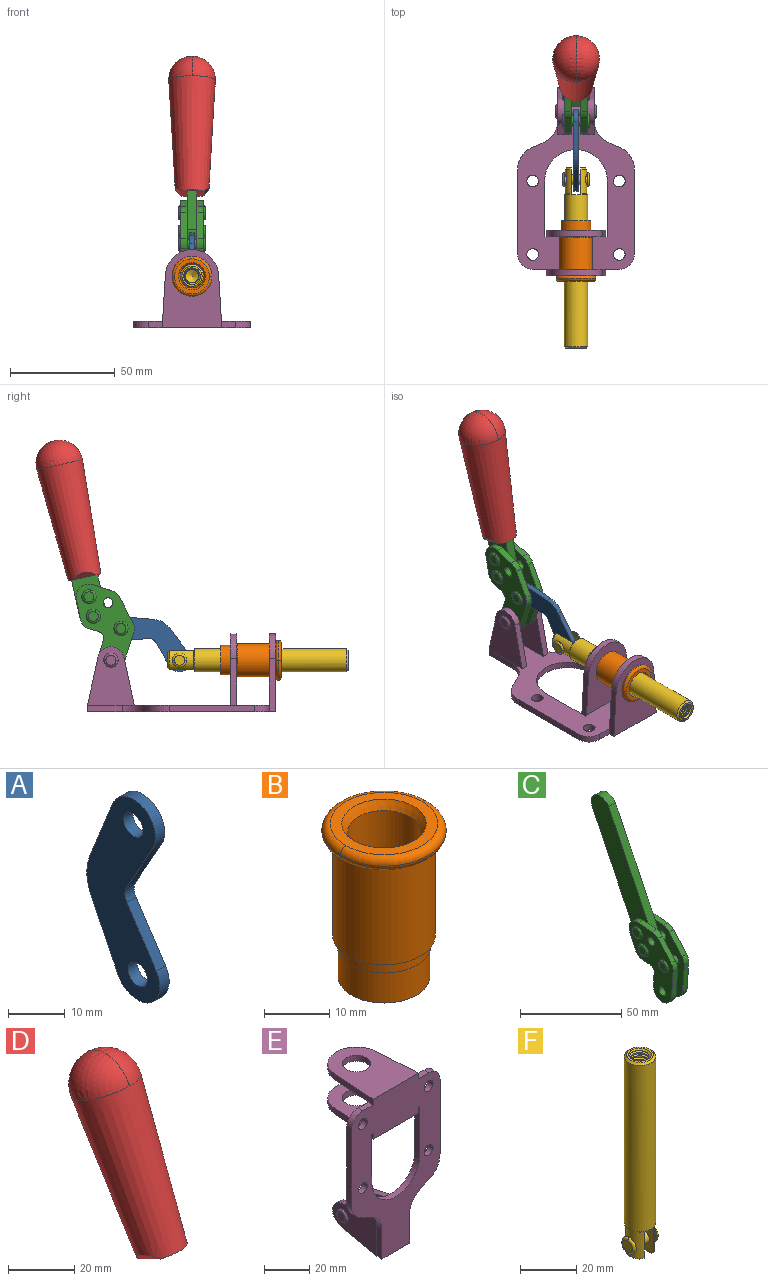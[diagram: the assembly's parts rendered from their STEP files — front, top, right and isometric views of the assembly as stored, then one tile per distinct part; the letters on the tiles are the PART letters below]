
ASSEMBLY  parts=6 mates=6
PART A: 12 faces, bbox 2.3x18.2x42.8 mm
  f0: cylinder r=2.4mm len=4.8mm, axis (1,0,0), area 34.9mm2, adj f4,f11
  f1: cylinder r=10.41mm len=8.47mm, axis (1,0,0), area 20.2mm2, adj f4,f9,f10,f11
  f2: cylinder r=3.05mm len=3.16mm, axis (1,0,0), area 7.7mm2, adj f4,f6,f7,f11
  f3: cylinder r=2.4mm len=4.8mm, axis (1,0,0), area 34.9mm2, adj f4,f11
  f4: plane 42.81x18.23mm, normal (-1,0,0), area 414.1mm2, adj f0,f1,f2,f3,f5,f6,f7,f8
  f5: cylinder r=5.54mm len=10.67mm, axis (1,0,0), area 41.8mm2, adj f4,f6,f10,f11
  f6: plane 11.66x6.53mm, normal (0,-0.87,-0.49), area 30.9mm2, adj f2,f4,f5,f11
  f7: plane 11.17x7.33mm, normal (0,-0.84,0.55), area 30.9mm2, adj f2,f4,f8,f11
  f8: cylinder r=5.54mm len=10.51mm, axis (1,0,0), area 41.8mm2, adj f4,f7,f9,f11
  f9: plane 13.67x6.67mm, normal (0,0.9,-0.44), area 35.1mm2, adj f1,f4,f8,f11
  f10: plane 14.1x5.7mm, normal (0,0.93,0.37), area 35.1mm2, adj f1,f4,f5,f11
  f11: plane 42.81x18.23mm, normal (1,0,0), area 414.1mm2, adj f0,f1,f2,f3,f5,f6,f7,f8
PART B: 15 faces, bbox 20.6x20.6x28.7 mm
  f0: torus R=8.26mm, axis (0,0,1), area 56.8mm2, adj f1,f10,f12
  f1: torus R=8.26mm, axis (0,0,1), area 56.8mm2, adj f0,f6,f13
  f2: cylinder r=5.59mm len=25.91mm, axis (0,0,1), area 909.6mm2, adj f3,f4
  f3: cone r=6.86mm half-angle=45deg, axis (0,0,-1), area 70.2mm2, adj f2,f14
  f4: cone r=6.47mm half-angle=30deg, axis (0,0,1), area 66.7mm2, adj f2,f13
  f5: cylinder r=7.04mm len=14.07mm, axis (0,0,1), area 252.6mm2, adj f11,f14
  f6: torus R=8.26mm, axis (0,0,1), area 56.8mm2, adj f1,f12,f13
  f7: cylinder r=7.16mm len=14.33mm, axis (0,0,1), area 91.5mm2, adj f9,f11
  f8: cylinder r=7.86mm len=18.42mm, axis (0,0,1), area 909.6mm2, adj f9,f10
  f9: plane 15.72x15.72mm, normal (0,0,-1), area 33mm2, adj f7,f8
  f10: plane 16.51x16.51mm, normal (0,0,-1), area 19.9mm2, adj f0,f8,f12
  f11: plane 14.33x14.33mm, normal (0,0,-1), area 5.7mm2, adj f5,f7
  f12: torus R=8.26mm, axis (0,0,1), area 56.8mm2, adj f0,f6,f10
  f13: plane 16.51x16.51mm, normal (0,0,1), area 82.7mm2, adj f1,f4,f6
  f14: plane 14.07x14.07mm, normal (0,0,-1), area 7.8mm2, adj f3,f5
PART C: 59 faces, bbox 12.9x60.2x99.6 mm
  f0: torus R=2.39mm, axis (-1,0,0), area 14.9mm2, adj f20,f43,f51
  f1: torus R=2.39mm, axis (-1,0,0), area 14.9mm2, adj f19,f42,f51
  f2: torus R=2.39mm, axis (-1,0,0), area 14.9mm2, adj f18,f35,f51
  f3: torus R=2.39mm, axis (-1,0,0), area 14.9mm2, adj f14,f17,f23
  f4: torus R=2.39mm, axis (-1,0,0), area 14.9mm2, adj f13,f16,f23
  f5: torus R=2.39mm, axis (-1,0,0), area 14.9mm2, adj f12,f15,f23
  f6: cylinder r=2.39mm len=4.78mm, axis (1,0,0), area 46.5mm2, adj f48,f50,f51
  f7: cylinder r=2.39mm len=4.78mm, axis (1,0,0), area 46.5mm2, adj f50,f51
  f8: cylinder r=6.35mm len=12.68mm, axis (1,0,0), area 61.8mm2, adj f38,f39,f50,f51
  f9: cylinder r=2.39mm len=4.78mm, axis (-1,0,0), area 70.5mm2, adj f46,f50
  f10: cylinder r=2.39mm len=4.78mm, axis (-1,0,0), area 46.5mm2, adj f23,f45,f46
  f11: cylinder r=2.39mm len=4.78mm, axis (-1,0,0), area 46.5mm2, adj f23,f46
  f12: plane 4.78x4.78mm, normal (1,0,0), area 17.9mm2, adj f5,f15
  f13: plane 4.78x4.78mm, normal (1,0,0), area 17.9mm2, adj f4,f16
  f14: plane 4.78x4.78mm, normal (1,0,0), area 17.9mm2, adj f3,f17
  f15: torus R=2.39mm, axis (-1,0,0), area 14.9mm2, adj f5,f12,f23
  f16: torus R=2.39mm, axis (-1,0,0), area 14.9mm2, adj f4,f13,f23
  f17: torus R=2.39mm, axis (-1,0,0), area 14.9mm2, adj f3,f14,f23
  f18: plane 4.78x4.78mm, normal (-1,0,0), area 17.9mm2, adj f2,f35
  f19: plane 4.78x4.78mm, normal (-1,0,0), area 17.9mm2, adj f1,f42
  f20: plane 4.78x4.78mm, normal (-1,0,0), area 17.9mm2, adj f0,f43
  f21: plane 2.26x0.2mm, normal (1,0,0), area 0.2mm2, adj f31,f44
  f22: plane 2.26x0.2mm, normal (-1,0,0), area 0.2mm2, adj f41,f44
  f23: plane 39.37x30.77mm, normal (1,0,0), area 565.5mm2, adj f3,f4,f5,f10,f11,f15,f16,f17
  f24: cylinder r=6.1mm len=4.15mm, axis (-1,0,0), area 14.7mm2, adj f23,f25,f32,f46
  f25: plane 10.25x9.01mm, normal (0,-0.75,0.66), area 42.3mm2, adj f23,f24,f26,f46
  f26: cylinder r=6.35mm len=4.64mm, axis (-1,0,0), area 15.6mm2, adj f23,f25,f27,f46
  f27: plane 15.84x3.1mm, normal (0,-1,-0.07), area 49.2mm2, adj f23,f26,f28,f46
  f28: cylinder r=6.35mm len=12.68mm, axis (-1,0,0), area 61.8mm2, adj f23,f27,f29,f46
  f29: plane 8.11x3.1mm, normal (0,1,0.07), area 25.2mm2, adj f23,f28,f30,f46
  f30: cylinder r=3.05mm len=3.25mm, axis (-1,0,0), area 14.8mm2, adj f23,f29,f31,f46
  f31: plane 5.99x3.1mm, normal (0,0.07,-1), area 18.6mm2, adj f21,f23,f30,f44,f46
  f32: plane 9.5x3.1mm, normal (0,-0.07,1), area 29.5mm2, adj f23,f24,f33,f46,f47
  f33: cylinder r=6.1mm len=8.63mm, axis (-1,0,0), area 39.1mm2, adj f23,f32,f34,f47
  f34: plane 8.65x3.96mm, normal (0,0.91,-0.42), area 29.5mm2, adj f23,f33,f44,f47
  f35: torus R=2.39mm, axis (-1,0,0), area 14.9mm2, adj f2,f18,f51
  f36: plane 10.25x9.01mm, normal (0,-0.75,0.66), area 42.3mm2, adj f37,f49,f50,f51
  f37: cylinder r=6.35mm len=4.64mm, axis (1,0,0), area 15.6mm2, adj f36,f38,f50,f51
  f38: plane 15.84x3.1mm, normal (0,-1,-0.07), area 49.2mm2, adj f8,f37,f50,f51
  f39: plane 8.11x3.1mm, normal (0,1,0.07), area 25.2mm2, adj f8,f40,f50,f51
  f40: cylinder r=3.05mm len=3.25mm, axis (1,0,0), area 14.8mm2, adj f39,f41,f50,f51
  f41: plane 5.99x3.1mm, normal (0,0.07,-1), area 18.6mm2, adj f22,f40,f44,f50,f51
  f42: torus R=2.39mm, axis (-1,0,0), area 14.9mm2, adj f1,f19,f51
  f43: torus R=2.39mm, axis (-1,0,0), area 14.9mm2, adj f0,f20,f51
  f44: cylinder r=6.35mm len=12.12mm, axis (-1,0,0), area 128.9mm2, adj f21,f22,f23,f31,f34,f41,f46,f47
  f45: plane 2.65x1.35mm, normal (1,0,0), area 1mm2, adj f10,f55
  f46: plane 39.08x20.42mm, normal (-1,0,0), area 412.5mm2, adj f9,f10,f11,f24,f25,f26,f27,f28
  f47: plane 77.62x39.82mm, normal (1,0,0), area 850mm2, adj f32,f33,f34,f44,f53,f54,f55
  f48: plane 2.65x1.35mm, normal (-1,0,0), area 1mm2, adj f6,f55
  f49: cylinder r=6.1mm len=4.15mm, axis (1,0,0), area 14.7mm2, adj f36,f50,f51,f56
  f50: plane 39.08x20.42mm, normal (1,0,0), area 412.5mm2, adj f6,f7,f8,f9,f36,f37,f38,f39
  f51: plane 39.37x30.77mm, normal (-1,0,0), area 565.5mm2, adj f0,f1,f2,f6,f7,f8,f35,f36
  f52: plane 8.65x3.96mm, normal (0,0.91,-0.42), area 29.5mm2, adj f44,f51,f57,f58
  f53: plane 68.49x33.4mm, normal (0,0.9,-0.44), area 358.1mm2, adj f44,f47,f54,f58
  f54: cylinder r=6.35mm len=12.06mm, axis (1,0,0), area 93.7mm2, adj f47,f53,f55,f58
  f55: plane 68.49x33.4mm, normal (0,-0.9,0.44), area 358.1mm2, adj f44,f45,f46,f47,f48,f50,f54,f58
  f56: plane 9.5x3.1mm, normal (0,-0.07,1), area 29.5mm2, adj f49,f50,f51,f57,f58
  f57: cylinder r=6.1mm len=8.63mm, axis (1,0,0), area 39.1mm2, adj f51,f52,f56,f58
  f58: plane 77.62x39.82mm, normal (-1,0,0), area 850mm2, adj f44,f52,f53,f54,f55,f56,f57
PART D: 11 faces, bbox 22.3x42.6x64.5 mm
  f0: sphere r=11.13mm, area 411.4mm2, adj f1,f8
  f1: cone r=11.11mm half-angle=3.3deg, axis (0,0.44,0.9), area 3251.8mm2, adj f0,f7,f8,f9,f10
  f2: cylinder r=6.16mm len=11.7mm, axis (1,0,0), area 89.5mm2, adj f3,f4,f5,f6
  f3: plane 60.23x36.75mm, normal (-1,0,0), area 763.6mm2, adj f2,f4,f6,f10
  f4: plane 51.37x25.05mm, normal (0,0.9,-0.44), area 264.2mm2, adj f2,f3,f5,f10
  f5: plane 60.23x36.75mm, normal (1,0,0), area 763.6mm2, adj f2,f4,f6,f10
  f6: plane 51.37x25.05mm, normal (0,-0.9,0.44), area 264.2mm2, adj f2,f3,f5,f10
  f7: plane 9.95x5.95mm, normal (0.71,-0.31,-0.64), area 25.8mm2, adj f1,f10
  f8: sphere r=11.13mm, area 411.4mm2, adj f0,f1
  f9: plane 9.95x5.95mm, normal (-0.71,-0.31,-0.64), area 25.8mm2, adj f1,f10
  f10: plane 14.27x11.38mm, normal (0,-0.44,-0.9), area 106.7mm2, adj f1,f3,f4,f5,f6,f7,f9
PART E: 55 faces, bbox 55.7x37.4x89.8 mm
  f0: torus R=2.41mm, axis (-1,0,0), area 15mm2, adj f11,f15,f25
  f1: torus R=2.41mm, axis (-1,0,0), area 15mm2, adj f10,f12,f22
  f2: cylinder r=2.78mm len=5.56mm, axis (0,-1,0), area 54.2mm2, adj f30,f54
  f3: cylinder r=14.99mm len=29.97mm, axis (0,-1,0), area 145.9mm2, adj f30,f49,f53,f54
  f4: cylinder r=2.78mm len=5.56mm, axis (0,-1,0), area 54.2mm2, adj f30,f54
  f5: cylinder r=2.78mm len=5.56mm, axis (0,-1,0), area 54.2mm2, adj f30,f54
  f6: cylinder r=2.78mm len=5.56mm, axis (0,-1,0), area 54.2mm2, adj f30,f54
  f7: cylinder r=6.35mm len=12.7mm, axis (0,0,1), area 123.6mm2, adj f27,f51
  f8: cylinder r=6.35mm len=12.7mm, axis (0,0,-1), area 124.7mm2, adj f21,f35
  f9: cylinder r=2.41mm len=11.18mm, axis (-1,0,0), area 169.4mm2, adj f16,f19
  f10: plane 4.83x4.83mm, normal (1,0,0), area 18.3mm2, adj f1,f12
  f11: plane 4.83x4.83mm, normal (-1,0,0), area 18.3mm2, adj f0,f15
  f12: torus R=2.41mm, axis (-1,0,0), area 15mm2, adj f1,f10,f22
  f13: cylinder r=6.35mm len=12.41mm, axis (1,0,0), area 53.4mm2, adj f18,f19,f22,f23
  f14: cylinder r=6.35mm len=12.41mm, axis (-1,0,0), area 53.4mm2, adj f16,f17,f24,f25
  f15: torus R=2.41mm, axis (-1,0,0), area 15mm2, adj f0,f11,f25
  f16: plane 27.86x22.35mm, normal (1,0,0), area 425.4mm2, adj f9,f14,f17,f24,f30
  f17: plane 22.86x4.97mm, normal (0,0.21,0.98), area 72.5mm2, adj f14,f16,f25,f30
  f18: plane 22.86x4.97mm, normal (0,0.21,0.98), area 72.5mm2, adj f13,f19,f22,f30
  f19: plane 27.86x22.35mm, normal (-1,0,0), area 425.4mm2, adj f9,f13,f18,f23,f30
  f20: cylinder r=12.7mm len=25.35mm, axis (0,0,-1), area 119.8mm2, adj f21,f34,f35,f36
  f21: plane 34.21x28.07mm, normal (0,0,-1), area 702.4mm2, adj f8,f20,f30,f34,f36
  f22: plane 27.96x22.45mm, normal (1,0,0), area 407.2mm2, adj f1,f12,f13,f18,f23,f30,f42,f43
  f23: plane 22.86x4.97mm, normal (0,0.21,-0.98), area 72.5mm2, adj f13,f19,f22,f44
  f24: plane 22.86x4.97mm, normal (0,0.21,-0.98), area 72.5mm2, adj f14,f16,f25,f44
  f25: plane 27.86x22.35mm, normal (-1,0,0), area 407.1mm2, adj f0,f14,f15,f17,f24,f30,f45,f46
  f26: plane 3.1x0.95mm, normal (0,0,-1), area 2.7mm2, adj f30,f49,f50,f54
  f27: plane 34.21x28.07mm, normal (0,0,1), area 702.4mm2, adj f7,f28,f30,f50,f52
  f28: cylinder r=12.7mm len=25.35mm, axis (0,0,1), area 118.8mm2, adj f27,f50,f51,f52
  f29: plane 3.1x0.95mm, normal (0,0,-1), area 2.7mm2, adj f30,f52,f53,f54
  f30: plane 86.54x55.63mm, normal (0,1,0), area 2362.9mm2, adj f2,f3,f4,f5,f6,f16,f17,f18
  f31: plane 40.56x3.1mm, normal (-1,0,0), area 125.7mm2, adj f30,f32,f48,f54
  f32: cylinder r=7.11mm len=7.11mm, axis (0,-1,0), area 34.6mm2, adj f30,f31,f33,f54
  f33: plane 6.67x3.1mm, normal (0,0,1), area 20.4mm2, adj f30,f32,f34,f54
  f34: plane 25.39x3.13mm, normal (-1,0.06,0), area 79.5mm2, adj f20,f21,f33,f35,f54
  f35: plane 37.31x28.45mm, normal (0,0,1), area 789.9mm2, adj f8,f20,f34,f36,f54
  f36: plane 25.39x3.13mm, normal (1,0.06,0), area 79.5mm2, adj f20,f21,f35,f37,f54
  f37: plane 6.67x3.1mm, normal (0,0,1), area 20.4mm2, adj f30,f36,f38,f54
  f38: cylinder r=7.11mm len=7.11mm, axis (0,-1,0), area 34.6mm2, adj f30,f37,f39,f54
  f39: plane 40.56x3.1mm, normal (1,0,0), area 125.7mm2, adj f30,f38,f40,f54
  f40: cylinder r=11.18mm len=10.16mm, axis (0,-1,0), area 39.5mm2, adj f30,f39,f41,f54
  f41: plane 6.09x3.1mm, normal (0.42,0,-0.91), area 20.8mm2, adj f30,f40,f42,f54
  f42: cylinder r=11.18mm len=9.41mm, axis (0,-1,0), area 37.2mm2, adj f22,f30,f41,f43,f54
  f43: plane 16.5x3.1mm, normal (1,0,0), area 51.1mm2, adj f22,f42,f44,f54
  f44: plane 17.37x3.1mm, normal (0,0,-1), area 53.8mm2, adj f23,f24,f30,f43,f45,f54
  f45: plane 16.5x3.1mm, normal (-1,0,0), area 51.1mm2, adj f25,f44,f46,f54
  f46: cylinder r=11.18mm len=9.41mm, axis (0,-1,0), area 37.2mm2, adj f25,f30,f45,f47,f54
  f47: plane 6.09x3.1mm, normal (-0.42,0,-0.91), area 20.8mm2, adj f30,f46,f48,f54
  f48: cylinder r=11.18mm len=10.16mm, axis (0,-1,0), area 39.5mm2, adj f30,f31,f47,f54
  f49: plane 26.54x3.1mm, normal (-1,0,0), area 82.3mm2, adj f3,f26,f30,f54
  f50: plane 25.39x3.1mm, normal (1,0.06,0), area 78.8mm2, adj f26,f27,f28,f51,f54
  f51: plane 37.31x28.45mm, normal (0,0,-1), area 789.9mm2, adj f7,f28,f50,f52,f54
  f52: plane 25.39x3.1mm, normal (-1,0.06,0), area 78.8mm2, adj f27,f28,f29,f51,f54
  f53: plane 26.54x3.1mm, normal (1,0,0), area 82.3mm2, adj f3,f29,f30,f54
  f54: plane 89.66x55.63mm, normal (0,-1,0), area 2678.5mm2, adj f2,f3,f4,f5,f6,f26,f29,f31
PART F: 48 faces, bbox 12.6x11.1x86.1 mm
  f0: torus R=2.41mm, axis (-1,0,0), area 15mm2, adj f30,f32,f34
  f1: torus R=2.41mm, axis (-1,0,0), area 15mm2, adj f29,f31,f33
  f2: cylinder r=5.54mm len=72.39mm, axis (0,0,1), area 2518.5mm2, adj f3,f4,f42,f43
  f3: cone r=5.54mm half-angle=45deg, axis (0,0,1), area 7.6mm2, adj f2,f5,f41
  f4: cone r=5.54mm half-angle=45deg, axis (0,0,-1), area 34.9mm2, adj f2,f39
  f5: cylinder r=5.08mm len=11.48mm, axis (0,0,1), area 108.3mm2, adj f3,f7,f8,f41
  f6: cylinder r=2.41mm len=4.83mm, axis (-1,0,0), area 71.2mm2, adj f40,f41
  f7: cylinder r=2.41mm len=4.83mm, axis (-1,0,0), area 7.6mm2, adj f5,f34
  f8: cone r=5.08mm half-angle=45deg, axis (0,0,1), area 10.6mm2, adj f5,f37,f41
  f9: cone r=3.98mm half-angle=45deg, axis (0,0,1), area 17.6mm2, adj f27,f39,f45,f46,f47
  f10: cylinder r=2.41mm len=4.83mm, axis (-1,0,0), area 7.6mm2, adj f33,f38
  f11: cylinder r=3.2mm len=6.4mm, axis (0,0,1), area 78.4mm2, adj f12,f28,f44,f45,f47
  f12: cylinder r=3.2mm len=6.4mm, axis (0,0,1), area 10.5mm2, adj f11,f13,f45,f47
  f13: cylinder r=3.2mm len=6.4mm, axis (0,0,1), area 10.5mm2, adj f12,f14,f45,f47
  f14: cylinder r=3.2mm len=6.4mm, axis (0,0,1), area 10.5mm2, adj f13,f15,f45,f47
  f15: cylinder r=3.2mm len=6.4mm, axis (0,0,1), area 10.5mm2, adj f14,f16,f45,f47
  f16: cylinder r=3.2mm len=6.4mm, axis (0,0,1), area 10.5mm2, adj f15,f17,f45,f47
  f17: cylinder r=3.2mm len=6.4mm, axis (0,0,1), area 10.5mm2, adj f16,f18,f45,f47
  f18: cylinder r=3.2mm len=6.4mm, axis (0,0,1), area 10.5mm2, adj f17,f19,f45,f47
  f19: cylinder r=3.2mm len=6.4mm, axis (0,0,1), area 10.5mm2, adj f18,f20,f45,f47
  f20: cylinder r=3.2mm len=6.4mm, axis (0,0,1), area 10.5mm2, adj f19,f21,f45,f47
  f21: cylinder r=3.2mm len=6.4mm, axis (0,0,1), area 10.5mm2, adj f20,f22,f45,f47
  f22: cylinder r=3.2mm len=6.4mm, axis (0,0,1), area 10.5mm2, adj f21,f23,f45,f47
  f23: cylinder r=3.2mm len=6.4mm, axis (0,0,1), area 10.5mm2, adj f22,f24,f45,f47
  f24: cylinder r=3.2mm len=6.4mm, axis (0,0,1), area 10.5mm2, adj f23,f25,f45,f47
  f25: cylinder r=3.2mm len=6.4mm, axis (0,0,1), area 10.5mm2, adj f24,f26,f45,f47
  f26: cylinder r=3.2mm len=6.4mm, axis (0,0,1), area 10.5mm2, adj f25,f27,f45,f47
  f27: cylinder r=3.2mm len=6.4mm, axis (0,0,1), area 7.4mm2, adj f9,f26,f45,f47
  f28: cone r=3.2mm half-angle=60deg, axis (0,0,1), area 37.2mm2, adj f11
  f29: plane 4.83x4.83mm, normal (-1,0,0), area 18.3mm2, adj f1,f31
  f30: plane 4.83x4.83mm, normal (1,0,0), area 18.3mm2, adj f0,f32
  f31: torus R=2.41mm, axis (-1,0,0), area 15mm2, adj f1,f29,f33
  f32: torus R=2.41mm, axis (-1,0,0), area 15mm2, adj f0,f30,f34
  f33: plane 6.83x6.83mm, normal (1,0,0), area 18.3mm2, adj f1,f10,f31
  f34: plane 6.83x6.83mm, normal (-1,0,0), area 18.3mm2, adj f0,f7,f32
  f35: cone r=5.08mm half-angle=45deg, axis (0,0,1), area 10.6mm2, adj f36,f38,f40
  f36: plane 7.25x1.97mm, normal (0,0,-1), area 10mm2, adj f35,f40
  f37: plane 7.25x1.97mm, normal (0,0,-1), area 10mm2, adj f8,f41
  f38: cylinder r=5.08mm len=11.48mm, axis (0,0,1), area 108.3mm2, adj f10,f35,f40,f42
  f39: plane 9.55x9.55mm, normal (0,0,1), area 22mm2, adj f4,f9
  f40: plane 12.76x10.09mm, normal (1,0,0), area 95.7mm2, adj f6,f35,f36,f38,f42,f43
  f41: plane 12.76x10.09mm, normal (-1,0,0), area 95.7mm2, adj f3,f5,f6,f8,f37,f43
  f42: cone r=5.54mm half-angle=45deg, axis (0,0,1), area 7.6mm2, adj f2,f38,f40
  f43: plane 11.07x4.7mm, normal (0,0,-1), area 50.4mm2, adj f2,f40,f41
  f44: plane 0.89x0.62mm, normal (-1,0,0), area 0.3mm2, adj f11,f45,f46,f47
  f45: bspline ~24.8x7.63mm, area 266.6mm2, adj f9,f11,f12,f13,f14,f15,f16,f17
  f46: bspline ~24.87x7.63mm, area 73.6mm2, adj f9,f44,f45,f47
  f47: bspline ~24.98x7.63mm, area 272.5mm2, adj f9,f11,f12,f13,f14,f15,f16,f17
PLACE A rot(axis=(1,0,0),120.5deg) t=(0,34.38,11.25)mm
PLACE B rot(axis=(1,0,0),90deg) t=(0,9.14,0)mm
PLACE C rot(axis=(1,0,0),13.5deg) t=(0,9.82,50.09)mm
PLACE D rot(axis=(1,0,0),13.5deg) t=(0.04,9.82,50.09)mm
PLACE E rot(axis=(1,0,0),90deg) t=(0,9.14,0)mm fixed
PLACE F rot(axis=(1,0,0),90deg) t=(0,24.04,0)mm
MATE slider F.f2 <-> E.f7  axis (0,-1,0) through (0,-34.74,24.61)mm
MATE revolute E.f0 <-> C.f7  axis (-1,0,0) through (0,41.23,24.61)mm
MATE fastened B.f2 <-> E.f7  axis (0,1,0) through (0,-37.25,24.61)mm
MATE revolute A.f3 <-> C.f4  axis (1,0,0) through (0,36.47,39.76)mm
MATE revolute A.f5 <-> F.f6  axis (1,0,0) through (0,8.56,24.61)mm
MATE fastened D.f2 <-> C.f54  axis (-1,0,0) through (2.35,66.16,119.9)mm
